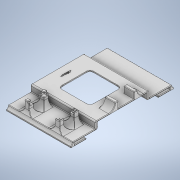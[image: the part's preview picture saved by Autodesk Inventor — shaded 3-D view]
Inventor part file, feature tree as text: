
AUTODESK INVENTOR PART (.ipt)
format: ipt  version: 2020 (Build 240168000, 168)  size: 1,018,368 bytes
history: native  units: in
note: dims shown in document units (in); Inventor stores cm internally (conversion verified against a paired STEP export)
features: sketch x14, extrude x13, fillet x13, emboss x1
ambient origin geometry x8: Origin, YZ Plane, XZ Plane, XY Plane, X Axis, Y Axis, Z Axis, Center Point
bodies: Solid1 (feature_tree)
feature tree (41):
  extrude  "Extrusion1"  Depth=3.1102in
  extrude  "Extrusion2"  Depth=0.0787in
  extrude  "Extrusion6"  TaperAngle=90.0deg  [1 undecoded]
  extrude  "Extrusion7"  Depth=1.8898in
  extrude  "Extrusion8"  Depth=0.0787in
  extrude  "Extrusion9"  Depth=0.0787in
  extrude  "Extrusion10"  Depth=0.3937in TaperAngle=0.0deg
  extrude  "Extrusion11"  Depth=0.0787in
  emboss  "Emboss1"
  extrude  "Extrusion12"  Depth=1.378in TaperAngle=0.0deg
  extrude  "Extrusion13"  Depth=0.1181in
  extrude  "Extrusion14"  Depth=0.1181in
  extrude  "Extrusion15"  Depth=0.0787in TaperAngle=0.0deg
  extrude  "Extrusion16"  Depth=0.3937in
  fillet  "Fillet9"  Radius=0.0394in
  fillet  "Fillet10"  Radius=0.1969in
  fillet  "Fillet11"  Radius=0.1969in
  fillet  "Fillet13"  Radius=0.3937in
  fillet  "Fillet16"  Radius=0.9843in
  fillet  "Fillet15"  Radius=0.9843in
  fillet  "Fillet17"  Radius=0.5118in
  fillet  "Fillet18"  Radius=1.0236in
  fillet  "Fillet19"  Radius=0.1969in
  fillet  "Fillet20"  Radius=0.1969in
  fillet  "Fillet22"  Radius=0.1969in
  fillet  "Fillet23"  Radius=0.1969in
  fillet  "Fillet24"  Radius=0.1969in
  sketch  "Sketch1"  dims[d0=3.937in d1=3.1102in]
  sketch  "Sketch2"  dims[d2=0.0787in d3=0.0in d4=0.9449in]
  sketch  "Sketch9"  dims[d5=0.9449in d6=90.0deg]
  sketch  "Sketch10"  dims[d7=1.8898in d8=1.8898in]
  sketch  "Sketch11"  dims[d9=0.3937in d10=0.0in d55=0.0787in]
  sketch  "Sketch12"  dims[d56=0.1575in d57=0.0787in]
  sketch  "Sketch14"  dims[d58=0.1575in d59=0.3937in d60=0.0in]
  sketch  "Sketch16"  dims[d61=0.0787in d62=0.0in d63=0.0787in]
  sketch  "Sketch18"  dims[d64=1.378in d65=0.0in d66=1.378in d67=0.0in]
  sketch  "Sketch19"  dims[d68=0.1181in d69=0.1181in]
  sketch  "Sketch20"  dims[d70=0.1181in d71=0.0in d73=0.1181in]
  sketch  "Sketch21"  dims[d74=0.1181in d75=0.0787in d76=0.0in]
  sketch  "Sketch23"  dims[d91=0.3937in d92=0.3937in d93=0.0394in d94=0.0in d95=0.1969in d96=0.1969in d97=0.3937in d98=0.0in d99=0.9843in d100=0.9843in d101=0.5118in d102=1.0236in d103=0.1969in d104=0.1969in d105=0.1969in d106=0.1969in d107=0.1969in]
  sketch  "Sketch24"  dims[d108=0.1969in d109=0.1969in d110=0.1969in d111=0.4724in d112=0.0in d113=0.1969in d114=0.0787in d115=0.0787in d116=0.1969in d117=0.0787in d118=0.0787in d119=0.2756in d120=0.0787in d121=0.0787in d122=0.2756in d123=0.0787in d124=0.2756in d125=0.5906in d126=0.0in d127=0.1969in d128=0.1969in d129=0.1969in d130=0.1969in d131=0.0787in d132=0.0in d133=0.0945in d134=0.0945in d135=0.0787in d136=0.0in d137=0.0315in d138=0.0787in d139=0.2362in d141=0.1969in d143=0.0315in d144=0.3937in d145=0.315in d146=0.0315in d147=0.0315in d148=0.0315in d150=0.0394in d151=0.0197in d152=0.1181in d21=0.1969in d22=0.0344in d23=0.1969in d24=0.0344in]
note: 1 required parameter value undecoded (feature->parameter linkage not recoverable at this tier; creation-order binding heuristic only, values carry confidence <= 0.55)
